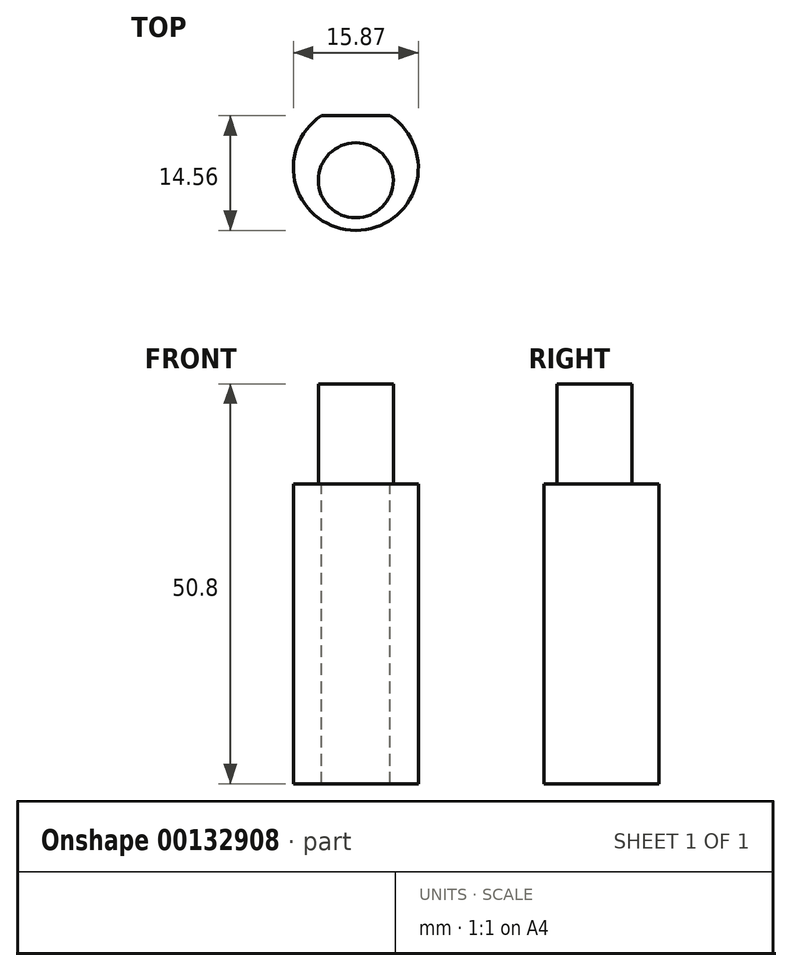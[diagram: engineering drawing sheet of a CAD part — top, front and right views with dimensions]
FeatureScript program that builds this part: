
annotation { "Feature Type Name" : "Feature", "Feature Type Description" : "" }
export const myFeature = defineFeature(function(context is Context, id is Id, definition is map)
    precondition{}
    {
        {
            var Q0;
            Q0=qCreatedBy(makeId("Top.planeOp"),FACE);
            var sketch = newSketch(context, id + "F0", { "sketchPlane" : qUnion([Q0])});
            skCircle(sketch, "E0", {"center": v(0, 0) * mm, "radius": 4.76 * mm});
            skArc(sketch, "E1", {"start": v(-4.37, 8.2) * mm, "mid": v(0, -6.36) * mm, "end": v(4.38, 8.2) * mm});
            skLineSegment(sketch, "E2", {"start": v(-4.37, 8.2) * mm, "end": v(4.38, 8.2) * mm});
            skPoint(sketch, "E3.orphan", {"position": v(0, 8.2) * mm});
            skSolve(sketch);
        }
        {
            var Q0;
            Q0=makeQuery(id+"F0.imprint","IMPRINT",FACE,{"disambiguationData":[TD([[makeQuery(id+"F0.imprint","IMPRINT",EDGE,{"derivedFrom":sQuery(id+"F0.wireOp",EDGE,"E0")}),1.0]])]});
            extrude(context, id + "F1", {"entities" : qUnion([Q0]), "depth" : 12.7 * mm});
        }
        {
            var Q0;
            Q0=makeQuery(id+"F0.imprint","IMPRINT",FACE,{"disambiguationData":[TD([[makeQuery(id+"F0.imprint","IMPRINT",EDGE,{"derivedFrom":sQuery(id+"F0.wireOp",EDGE,"E0")}),-1.0]])]});
            var Q1;
            Q1=makeQuery(id+"F0.imprint","IMPRINT",FACE,{"disambiguationData":[TD([[makeQuery(id+"F0.imprint","IMPRINT",EDGE,{"derivedFrom":sQuery(id+"F0.wireOp",EDGE,"E0")}),1.0]])]});
            extrude(context, id + "F2", {"entities" : qUnion([Q0, Q1]), "operationType" : NewBodyOperationType.ADD, "oppositeDirection" : true, "depth" : 38.1 * mm});
        }
    });
